# Revit family: Hager-Volta-IP30-Flush_mounted-syst-NoHosted-SE-en
name_source: partatom
category: Electrical Equipment
units: mm (PartAtom-declared; Revit-internal decimal feet)

## family parameters
Always vertical = Yes
Cut with Voids When Loaded = No
Panel Configuration = Two Columns, Circuits Across
Part Type = Panelboard
Room Calculation Point = No
Round Connector Dimension = Use Diameter
Shared = No
Work Plane-Based = Yes

## types (11) — shared parameters
Default Elevation = 1219 mm
EF000003 - Mounting method = EV000383 - Flush mounted (plaster)
EF000007 - Colour = EV000202 - White
EF000116 - RAL-number = 9010
EF000339 - Type of cover = EV004216 - Door
EF001088 - Extension possible = Yes
EF004462 - Type of closure = EV000154 - Other
EF005474 - Degree of protection (IP) = EV006410 - IP30
EF006244 - Transparent cover/door = No
EF006306 - With lock = No
EF009212 - Cover model = EV009916 - With notch
EF015941 - Signal passing door = No
HG000001 - Number of columns = 1
HG000002 - With door or cover = Yes
HG000003 - Range = Volta
HG000005 - Thickness = 3 mm  [stored 0.00984252 ft]
HG000006 - Flush mounted = Yes
HG000009 - Double swing door = No
HG000010 - Asymmetric doors = No
HG000011 - Empty rows from bottom = No
HG000017 - Distance between poles = 18 mm  [stored 0.0590551 ft]
Manufacturer = Hager
Type Comments = Volta
zero-valued in all types: HG000007 - Number of empty columns, HG000008 - Number of empty rows

## per-type parameters (varying)
| type | EF000008 - Width | EF000040 - Height | EF000049 - Depth | EF000118 - With mounting plate | EF000218 - Built-in depth | EF000266 - Number of rows | EF000332 - Built-in height | EF000846 - Built-in width | EF001062 - EMC-version | EF001131 - Internal depth | EF001134 - DIN-rail | EF001596 - Material housing | EF002950 - Width in number of modular spacings | EF015776 - Earthing terminal block | EF015777 - Neutral terminal block | HG000004 - Manufacturer reference | Model |
| Recessed mounted IP30 W348 H356 D94.5 12 Modular spacings - VU12NF | 348 mm | 356 mm | 94 mm | No | 90 mm | 1 | 321 mm | 335 mm | No | 92 mm | Yes | EV000154 - Other | 12 | No | No | VU12NF | VU12NF |
| Recessed mounted IP30 W348 H356 D94.5 12 Modular spacings - VU12NN | 348 mm | 356 mm | 94 mm | No | 90 mm | 1 | 321 mm | 335 mm | No | 92 mm | Yes | EV000139 - Plastic | 12 | Yes | Yes | VU12NN | VU12NN |
| Recessed mounted IP30 W348 H505.5 D94.5 12 Modular spacings - VU24NN | 348 mm | 506 mm | 94 mm | No | 90 mm | 2 | 470 mm | 335 mm | No | 92 mm | Yes | EV000139 - Plastic | 12 | Yes | Yes | VU24NN | VU24NN |
| Recessed mounted IP30 W348 H630.5 D94.5 12 Modular spacings - VU36NN | 348 mm | 630 mm | 94 mm | No | 90 mm | 3 | 595 mm | 335 mm | No | 92 mm | Yes | EV000139 - Plastic | 12 | Yes | Yes | VU36NN | VU36NN |
| Recessed mounted IP30 W348 H755.5 D94.5 12 Modular spacings - VU48NMB | 348 mm | 756 mm | 94 mm | Yes | 90 mm | 4 | 720 mm  [stored 2.3622 ft] | 335 mm | No | 92 mm | Yes | EV000154 - Other | 12 | Yes | No | VU48NMB | VU48NMB |
| Recessed mounted IP30 W348 H755.5 D94.5 12 Modular spacings - VU48NN | 348 mm | 756 mm | 94 mm | No | 90 mm | 4 | 720 mm  [stored 2.3622 ft] | 335 mm | No | 92 mm | Yes | EV000139 - Plastic | 12 | Yes | Yes | VU48NN | VU48NN |
| Recessed mounted IP30 W348 H880.5 D94.5 12 Modular spacings - VU60NN | 348 mm | 880 mm | 94 mm | Yes | 90 mm | 5 | 880 mm | 335 mm | No | 92 mm | Yes | EV000154 - Other | 12 | Yes | No | VU60NN | VU60NN |
| Recessed mounted IP30 W426 H286 D89 18 Modular spacings - VU118F | 426 mm  [stored 1.39764 ft] | 286 mm | 89 mm  [stored 0.291995 ft] | Yes | 82 mm  [stored 0.269029 ft] | 1 | 259 mm | 396 mm  [stored 1.29921 ft] | Yes | 82 mm  [stored 0.269029 ft] | No | EV000139 - Plastic | 18 | No | No | VU118F | VU118F |
| Recessed mounted IP30 W426 H411 D89 18 Modular spacings - VU218F | 426 mm  [stored 1.39764 ft] | 411 mm | 89 mm  [stored 0.291995 ft] | No | 82 mm  [stored 0.269029 ft] | 2 | 394 mm | 396 mm  [stored 1.29921 ft] | Yes | 82 mm  [stored 0.269029 ft] | No | EV000139 - Plastic | 18 | No | No | VU218F | VU218F |
| Recessed mounted IP30 W426 H536 D89 18 Modular spacings - VU318F | 426 mm  [stored 1.39764 ft] | 536 mm | 89 mm  [stored 0.291995 ft] | No | 82 mm  [stored 0.269029 ft] | 3 | 509 mm | 396 mm  [stored 1.29921 ft] | Yes | 0 mm  [stored 0 ft] | No | EV000139 - Plastic | 18 | No | No | VU318F | VU318F |
| Recessed mounted IP30 W426 H661 D89 18 Modular spacings - VU418F | 426 mm  [stored 1.39764 ft] | 661 mm  [stored 2.16864 ft] | 89 mm  [stored 0.291995 ft] | No | 82 mm  [stored 0.269029 ft] | 4 | 634 mm  [stored 2.08005 ft] | 396 mm  [stored 1.29921 ft] | Yes | 82 mm  [stored 0.269029 ft] | No | EV000139 - Plastic | 18 | No | No | VU418F | VU418F |

note: [stored X ft] marks values corroborated as IEEE doubles in the binary element streams (Revit-internal decimal feet)

## geometry (parser evidence)
native form markers: Sweep x14
no freeform markers — native parametric forms only
